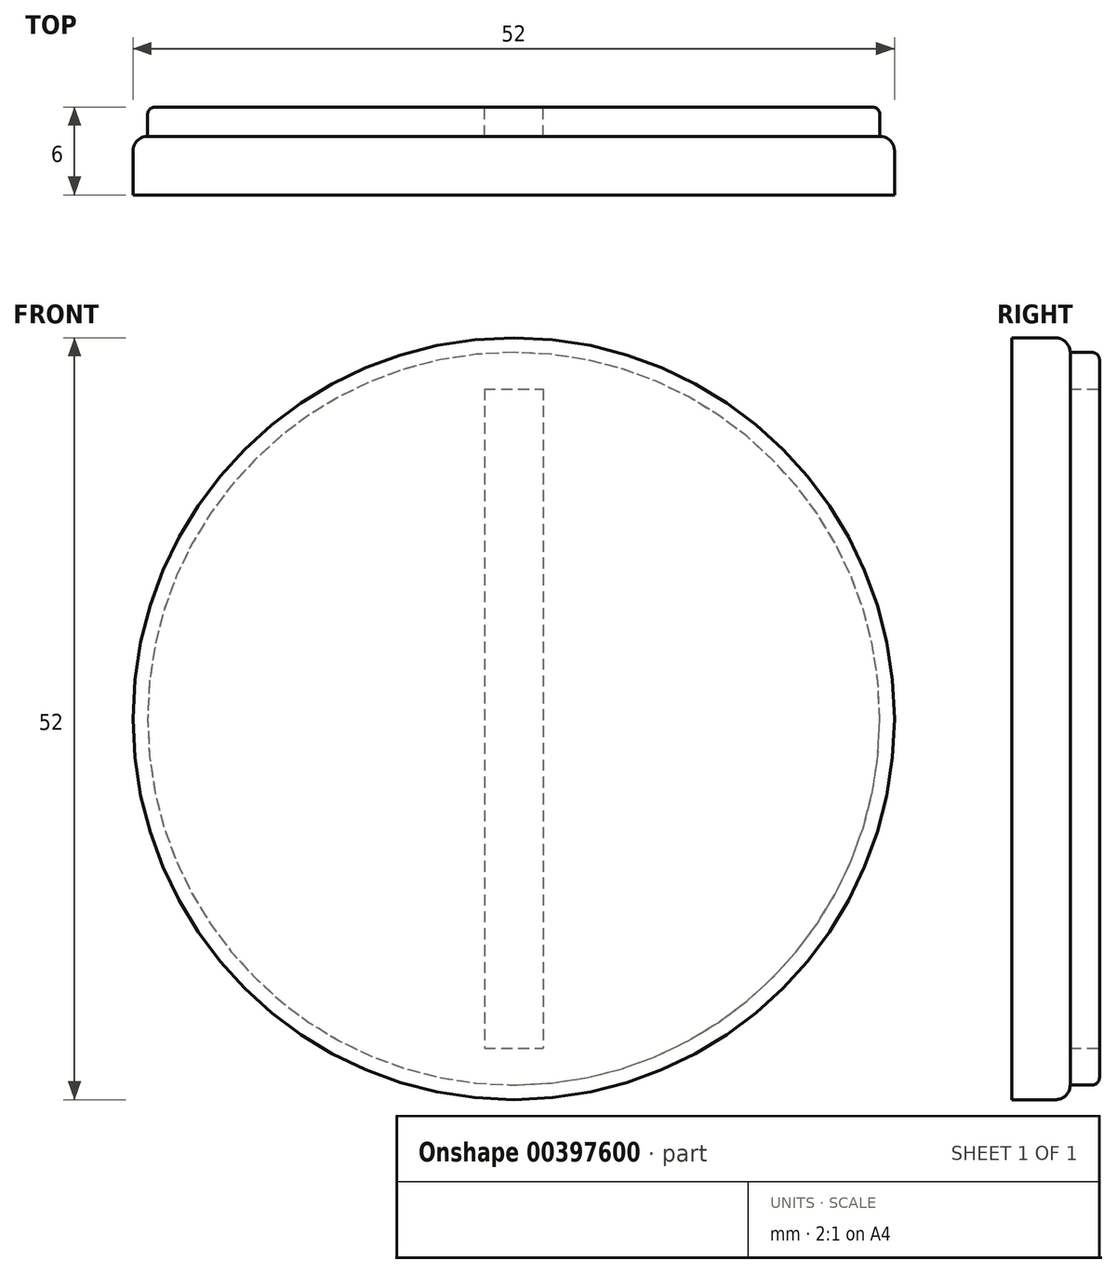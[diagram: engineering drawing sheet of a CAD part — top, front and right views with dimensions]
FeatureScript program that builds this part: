
annotation { "Feature Type Name" : "Feature", "Feature Type Description" : "" }
export const myFeature = defineFeature(function(context is Context, id is Id, definition is map)
    precondition{}
    {
        {
            var Q0;
            Q0=qCreatedBy(makeId("Front.planeOp"),FACE);
            var sketch = newSketch(context, id + "F0", { "sketchPlane" : qUnion([Q0])});
            skCircle(sketch, "E0", {"center": v(0, 0) * mm, "radius": 26 * mm});
            skSolve(sketch);
        }
        {
            var Q0;
            Q0=makeQuery(id+"F0.imprint","IMPRINT",FACE,{"disambiguationData":[TD([[makeQuery(id+"F0.imprint","IMPRINT",EDGE,{"derivedFrom":sQuery(id+"F0.wireOp",EDGE,"E0")}),1.0]])]});
            extrude(context, id + "F1", {"entities" : qUnion([Q0]), "depth" : 4 * mm});
        }
        {
            var Q0;
            Q0=makeQuery(id+"F1.opExtrude","CAP_FACE",FACE,{"disambiguationData":[OSD([sQuery(id+"F0.wireOp",EDGE,"E0")])],"isStart":true});
            var sketch = newSketch(context, id + "F2", { "sketchPlane" : qUnion([Q0])});
            skCircle(sketch, "E1", {"center": v(0, 0) * mm, "radius": 25 * mm});
            skSolve(sketch);
        }
        {
            var Q0;
            Q0=qSketchRegion(id+"F2",true);
            extrude(context, id + "F3", {"entities" : qUnion([Q0]), "operationType" : NewBodyOperationType.ADD, "depth" : 2 * mm});
        }
        {
            var Q0;
            Q0=makeQuery(id+"F1.opExtrude","CAP_EDGE",EDGE,{"disambiguationData":[OSD([sQuery(id+"F0.wireOp",EDGE,"E0")])],"isStart":true});
            fillet(context, id + "F4", {"entities" : qUnion([Q0]), "radius" : 1 * mm, "tangentPropagation" : true, "allowEdgeOverflow" : false});
        }
        {
            var Q0;
            Q0=makeQuery(id+"F3.opExtrude","CAP_EDGE",EDGE,{"disambiguationData":[OSD([sQuery(id+"F2.wireOp",EDGE,"E1")])],"isStart":false});
            fillet(context, id + "F5", {"entities" : qUnion([Q0]), "radius" : 0.5 * mm, "tangentPropagation" : true, "allowEdgeOverflow" : false});
        }
        {
            var Q0;
            Q0=makeQuery(id+"F3.opExtrude","CAP_FACE",FACE,{"disambiguationData":[OSD([sQuery(id+"F2.wireOp",EDGE,"E1")])],"isStart":false});
            var sketch = newSketch(context, id + "F6", { "sketchPlane" : qUnion([Q0])});
            skLineSegment(sketch, "E2.bottom", {"start": v(2, 22.5) * mm, "end": v(-2, 22.5) * mm});
            skLineSegment(sketch, "E2.top", {"start": v(2, -22.5) * mm, "end": v(-2, -22.5) * mm});
            skLineSegment(sketch, "E2.left", {"start": v(2, 22.5) * mm, "end": v(2, -22.5) * mm});
            skLineSegment(sketch, "E2.right", {"start": v(-2, 22.5) * mm, "end": v(-2, -22.5) * mm});
            skPoint(sketch, "E2.middle", {"position": v(0, 0) * mm});
            skSolve(sketch);
        }
        {
            var Q0;
            Q0=qSketchRegion(id+"F6",true);
            extrude(context, id + "F7", {"entities" : qUnion([Q0]), "operationType" : NewBodyOperationType.REMOVE, "oppositeDirection" : true, "depth" : 2 * mm});
        }
    });
